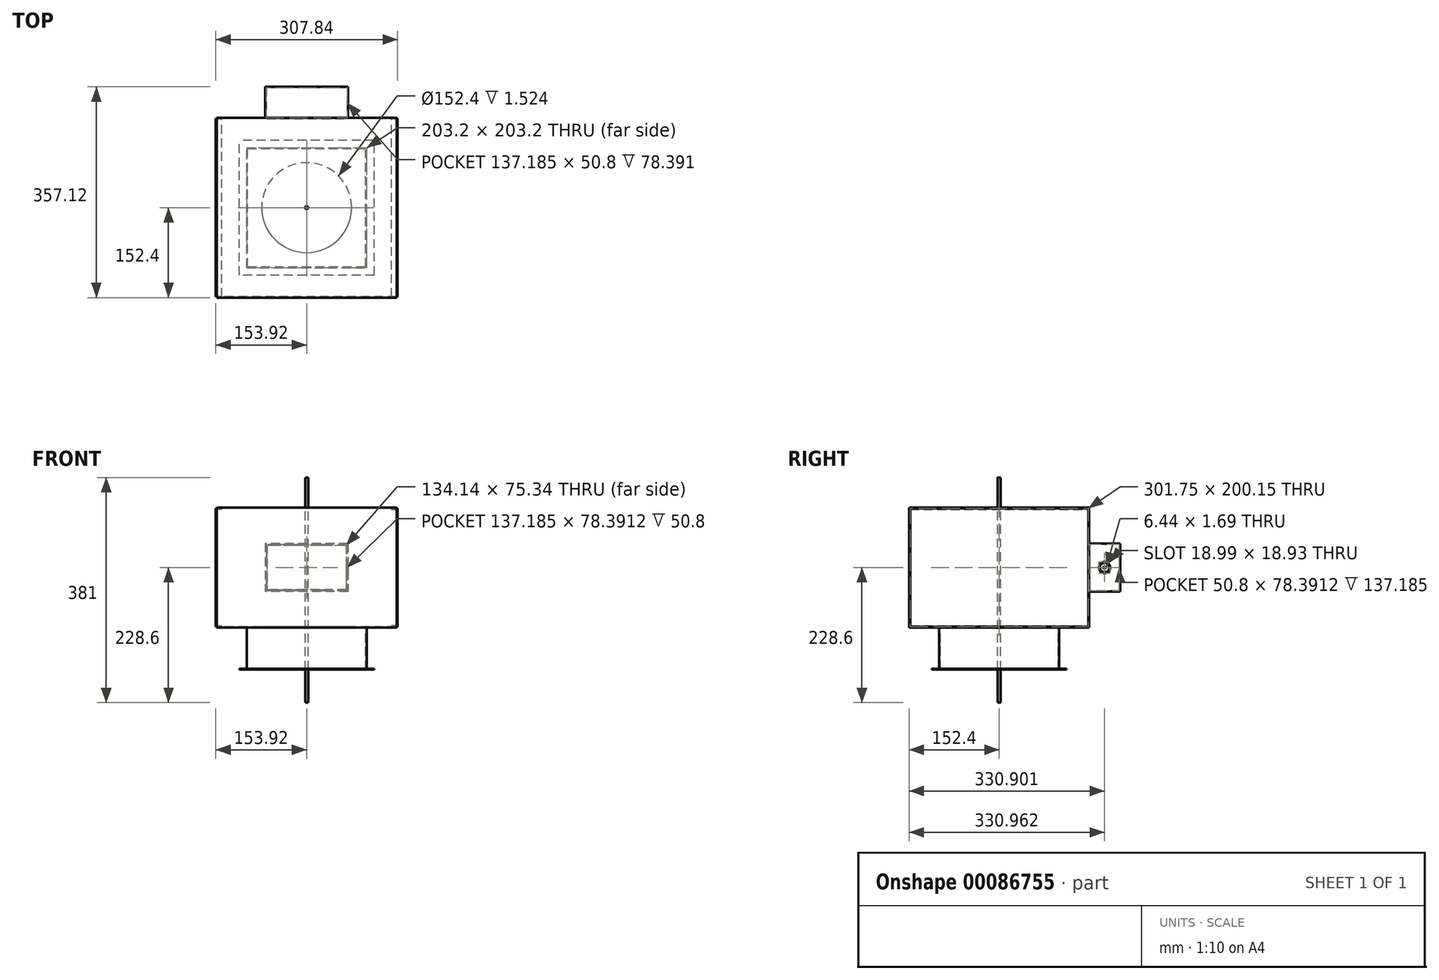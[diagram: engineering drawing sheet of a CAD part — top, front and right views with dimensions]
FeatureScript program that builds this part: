
annotation { "Feature Type Name" : "Feature", "Feature Type Description" : "" }
export const myFeature = defineFeature(function(context is Context, id is Id, definition is map)
    precondition{}
    {
        {
            var Q0;
            Q0=qCreatedBy(makeId("Right.planeOp"),FACE);
            var sketch = newSketch(context, id + "F0", { "sketchPlane" : qUnion([Q0])});
            skLineSegment(sketch, "E0.bottom", {"start": v(-152.4, 101.6) * mm, "end": v(152.4, 101.6) * mm});
            skLineSegment(sketch, "E0.top", {"start": v(-152.4, -101.6) * mm, "end": v(152.4, -101.6) * mm});
            skLineSegment(sketch, "E0.left", {"start": v(-152.4, 101.6) * mm, "end": v(-152.4, -101.6) * mm});
            skLineSegment(sketch, "E0.right", {"start": v(152.4, 101.6) * mm, "end": v(152.4, -101.6) * mm});
            skPoint(sketch, "E0.middle", {"position": v(0, 0) * mm});
            skLineSegment(sketch, "E1.0", {"start": v(-150.88, 100.08) * mm, "end": v(150.88, 100.08) * mm});
            skLineSegment(sketch, "E1.1", {"start": v(-150.88, 100.08) * mm, "end": v(-150.88, -100.08) * mm});
            skLineSegment(sketch, "E1.2", {"start": v(-150.88, -100.08) * mm, "end": v(150.88, -100.08) * mm});
            skLineSegment(sketch, "E1.3", {"start": v(150.88, 100.08) * mm, "end": v(150.88, -100.08) * mm});
            skSolve(sketch);
        }
        {
            var Q0;
            Q0 = qSketchRegion(id + "F0", true);
            extrude(context, id + "F1", {"entities" : qUnion([Q0]), "depth" : 304.8 * mm, "symmetric" : true});
        }
        {
            var Q0;
            Q0=qCreatedBy(makeId("Front.planeOp"),FACE);
            var sketch = newSketch(context, id + "F2", { "sketchPlane" : qUnion([Q0])});
            skLineSegment(sketch, "E2", {"start": v(-143.76, 100.08) * mm, "end": v(-153.92, 100.08) * mm});
            skLineSegment(sketch, "E3", {"start": v(-153.92, 100.08) * mm, "end": v(-153.92, -100.08) * mm});
            skLineSegment(sketch, "E4", {"start": v(-153.92, -100.08) * mm, "end": v(-143.76, -100.08) * mm});
            skLineSegment(sketch, "E5", {"start": v(0, 0) * mm, "end": v(-116.76, 0) * mm, "construction": true});
            skLineSegment(sketch, "E6", {"start": v(0, 0) * mm, "end": v(0, 86.38) * mm, "construction": true});
            skLineSegment(sketch, "E7.0", {"start": v(-152.4, -98.55) * mm, "end": v(-143.76, -98.55) * mm});
            skLineSegment(sketch, "E7.1", {"start": v(-152.4, 98.55) * mm, "end": v(-152.4, -98.55) * mm});
            skLineSegment(sketch, "E7.2", {"start": v(-143.76, 98.55) * mm, "end": v(-152.4, 98.55) * mm});
            skLineSegment(sketch, "E8", {"start": v(-143.76, 98.55) * mm, "end": v(-143.76, 100.08) * mm});
            skLineSegment(sketch, "E9", {"start": v(-143.76, -100.08) * mm, "end": v(-143.76, -98.55) * mm});
            skLineSegment(sketch, "E10.MirrorCS", {"start": v(143.76, 98.55) * mm, "end": v(143.76, 100.08) * mm});
            skLineSegment(sketch, "E11.MirrorCS", {"start": v(143.76, -100.08) * mm, "end": v(143.76, -98.55) * mm});
            skLineSegment(sketch, "E12.MirrorCS", {"start": v(152.4, -98.55) * mm, "end": v(143.76, -98.55) * mm});
            skLineSegment(sketch, "E13.MirrorCS", {"start": v(153.92, -100.08) * mm, "end": v(143.76, -100.08) * mm});
            skLineSegment(sketch, "E14.MirrorCS", {"start": v(143.76, 98.55) * mm, "end": v(152.4, 98.55) * mm});
            skLineSegment(sketch, "E15.MirrorCS", {"start": v(152.4, 98.55) * mm, "end": v(152.4, -98.55) * mm});
            skLineSegment(sketch, "E16.MirrorCS", {"start": v(143.76, 100.08) * mm, "end": v(153.92, 100.08) * mm});
            skLineSegment(sketch, "E17.MirrorCS", {"start": v(153.92, 100.08) * mm, "end": v(153.92, -100.08) * mm});
            skSolve(sketch);
        }
        {
            var Q0;
            Q0 = qSketchRegion(id + "F2", true);
            extrude(context, id + "F3", {"entities" : qUnion([Q0]), "depth" : 301.75 * mm, "symmetric" : true});
        }
        {
            var Q0;
            Q0=makeQuery(id+"F1.opExtrude","SWEPT_FACE",FACE,{"disambiguationData":[OSD([sQuery(id+"F0.wireOp",EDGE,"E0.top")])]});
            var sketch = newSketch(context, id + "F4", { "sketchPlane" : qUnion([Q0])});
            skCircle(sketch, "E18", {"center": v(0, 0) * mm, "radius": 76.2 * mm});
            skSolve(sketch);
        }
        {
            var Q0;
            Q0 = qSketchRegion(id + "F4", true);
            extrude(context, id + "F5", {"entities" : qUnion([Q0]), "operationType" : NewBodyOperationType.REMOVE, "endBound" : BoundingType.UP_TO_NEXT, "oppositeDirection" : true, "depth" : 25.4 * mm});
        }
        {
            var Q0;
            Q0=makeQuery(id+"F1.opExtrude","SWEPT_FACE",FACE,{"disambiguationData":[OSD([sQuery(id+"F0.wireOp",EDGE,"E0.top")])]});
            var sketch = newSketch(context, id + "F6", { "sketchPlane" : qUnion([Q0])});
            skLineSegment(sketch, "E19.bottom", {"start": v(-101.6, 101.6) * mm, "end": v(101.6, 101.6) * mm});
            skLineSegment(sketch, "E19.top", {"start": v(-101.6, -101.6) * mm, "end": v(101.6, -101.6) * mm});
            skLineSegment(sketch, "E19.left", {"start": v(-101.6, 101.6) * mm, "end": v(-101.6, -101.6) * mm});
            skLineSegment(sketch, "E19.right", {"start": v(101.6, 101.6) * mm, "end": v(101.6, -101.6) * mm});
            skPoint(sketch, "E19.middle", {"position": v(0, 0) * mm});
            skLineSegment(sketch, "E20.0", {"start": v(-100.08, 100.08) * mm, "end": v(100.08, 100.08) * mm});
            skLineSegment(sketch, "E20.1", {"start": v(-100.08, 100.08) * mm, "end": v(-100.08, -100.08) * mm});
            skLineSegment(sketch, "E20.2", {"start": v(-100.08, -100.08) * mm, "end": v(100.08, -100.08) * mm});
            skLineSegment(sketch, "E20.3", {"start": v(100.08, 100.08) * mm, "end": v(100.08, -100.08) * mm});
            skSolve(sketch);
        }
        {
            var Q0;
            Q0 = qSketchRegion(id + "F6", true);
            extrude(context, id + "F7", {"entities" : qUnion([Q0]), "operationType" : NewBodyOperationType.ADD, "depth" : 69.85 * mm});
        }
        {
            var Q0;
            Q0=makeQuery(id+"F7.opExtrude","CAP_FACE",FACE,{"disambiguationData":[OSD([sQuery(id+"F6.wireOp",EDGE,"E19.bottom"),sQuery(id+"F6.wireOp",EDGE,"E19.top"),sQuery(id+"F6.wireOp",EDGE,"E19.left"),sQuery(id+"F6.wireOp",EDGE,"E19.right"),sQuery(id+"F6.wireOp",EDGE,"E20.0"),sQuery(id+"F6.wireOp",EDGE,"E20.1"),sQuery(id+"F6.wireOp",EDGE,"E20.2"),sQuery(id+"F6.wireOp",EDGE,"E20.3")])],"isStart":false});
            var sketch = newSketch(context, id + "F8", { "sketchPlane" : qUnion([Q0])});
            skLineSegment(sketch, "E21.bottom", {"start": v(114.3, 114.3) * mm, "end": v(-114.3, 114.3) * mm});
            skLineSegment(sketch, "E21.top", {"start": v(114.3, -114.3) * mm, "end": v(-114.3, -114.3) * mm});
            skLineSegment(sketch, "E21.left", {"start": v(114.3, 114.3) * mm, "end": v(114.3, -114.3) * mm});
            skLineSegment(sketch, "E21.right", {"start": v(-114.3, 114.3) * mm, "end": v(-114.3, -114.3) * mm});
            skPoint(sketch, "E21.middle", {"position": v(0, 0) * mm});
            skLineSegment(sketch, "E22.bottom", {"start": v(100.08, 100.08) * mm, "end": v(-100.08, 100.08) * mm});
            skLineSegment(sketch, "E22.top", {"start": v(100.08, -100.08) * mm, "end": v(-100.08, -100.08) * mm});
            skLineSegment(sketch, "E22.left", {"start": v(100.08, 100.08) * mm, "end": v(100.08, -100.08) * mm});
            skLineSegment(sketch, "E22.right", {"start": v(-100.08, 100.08) * mm, "end": v(-100.08, -100.08) * mm});
            skSolve(sketch);
        }
        {
            var Q0;
            Q0 = qSketchRegion(id + "F8", true);
            extrude(context, id + "F9", {"entities" : qUnion([Q0]), "operationType" : NewBodyOperationType.ADD, "depth" : 1.52 * mm});
        }
        {
            var Q0;
            Q0=makeQuery(id+"F1.opExtrude","SWEPT_FACE",FACE,{"disambiguationData":[OSD([sQuery(id+"F0.wireOp",EDGE,"E0.right")])]});
            var sketch = newSketch(context, id + "F10", { "sketchPlane" : qUnion([Q0])});
            skLineSegment(sketch, "E23.bottom", {"start": v(-67.07, 37.67) * mm, "end": v(67.07, 37.67) * mm});
            skLineSegment(sketch, "E23.top", {"start": v(-67.07, -37.67) * mm, "end": v(67.07, -37.67) * mm});
            skLineSegment(sketch, "E23.left", {"start": v(-67.07, 37.67) * mm, "end": v(-67.07, -37.67) * mm});
            skLineSegment(sketch, "E23.right", {"start": v(67.07, 37.67) * mm, "end": v(67.07, -37.67) * mm});
            skPoint(sketch, "E23.middle", {"position": v(0, 0) * mm});
            skSolve(sketch);
        }
        {
            var Q0;
            Q0 = qSketchRegion(id + "F10", true);
            extrude(context, id + "F11", {"entities" : qUnion([Q0]), "operationType" : NewBodyOperationType.REMOVE, "endBound" : BoundingType.UP_TO_NEXT, "oppositeDirection" : true, "depth" : 25.4 * mm});
        }
        {
            var Q0;
            Q0=makeQuery(id+"F1.opExtrude","SWEPT_FACE",FACE,{"disambiguationData":[OSD([sQuery(id+"F0.wireOp",EDGE,"E0.right")])]});
            var sketch = newSketch(context, id + "F12", { "sketchPlane" : qUnion([Q0])});
            skLineSegment(sketch, "E24.bottom", {"start": v(-68.6, 39.2) * mm, "end": v(68.6, 39.2) * mm});
            skLineSegment(sketch, "E24.top", {"start": v(-68.6, -39.2) * mm, "end": v(68.6, -39.2) * mm});
            skLineSegment(sketch, "E24.left", {"start": v(-68.6, 39.2) * mm, "end": v(-68.6, -39.2) * mm});
            skLineSegment(sketch, "E24.right", {"start": v(68.6, 39.2) * mm, "end": v(68.6, -39.2) * mm});
            skPoint(sketch, "E24.middle", {"position": v(0, 0) * mm});
            skLineSegment(sketch, "E25.0", {"start": v(-70.12, 40.72) * mm, "end": v(70.12, 40.72) * mm});
            skLineSegment(sketch, "E25.1", {"start": v(-70.12, 40.72) * mm, "end": v(-70.12, -40.72) * mm});
            skLineSegment(sketch, "E25.2", {"start": v(-70.12, -40.72) * mm, "end": v(70.12, -40.72) * mm});
            skLineSegment(sketch, "E25.3", {"start": v(70.12, 40.72) * mm, "end": v(70.12, -40.72) * mm});
            skSolve(sketch);
        }
        {
            var Q0;
            Q0 = qSketchRegion(id + "F12", true);
            extrude(context, id + "F13", {"entities" : qUnion([Q0]), "operationType" : NewBodyOperationType.ADD, "depth" : 50.8 * mm});
        }
        {
            var Q0;
            Q0=makeQuery(id+"F13.opExtrude","CAP_FACE",FACE,{"disambiguationData":[OSD([sQuery(id+"F12.wireOp",EDGE,"E24.bottom"),sQuery(id+"F12.wireOp",EDGE,"E24.top"),sQuery(id+"F12.wireOp",EDGE,"E24.left"),sQuery(id+"F12.wireOp",EDGE,"E24.right"),sQuery(id+"F12.wireOp",EDGE,"E25.0"),sQuery(id+"F12.wireOp",EDGE,"E25.1"),sQuery(id+"F12.wireOp",EDGE,"E25.2"),sQuery(id+"F12.wireOp",EDGE,"E25.3")])],"isStart":false});
            var sketch = newSketch(context, id + "F14", { "sketchPlane" : qUnion([Q0])});
            skLineSegment(sketch, "E26.bottom", {"start": v(-70.12, 40.72) * mm, "end": v(70.12, 40.72) * mm});
            skLineSegment(sketch, "E26.top", {"start": v(-70.12, -40.72) * mm, "end": v(70.12, -40.72) * mm});
            skLineSegment(sketch, "E26.left", {"start": v(-70.12, 40.72) * mm, "end": v(-70.12, -40.72) * mm});
            skLineSegment(sketch, "E26.right", {"start": v(70.12, 40.72) * mm, "end": v(70.12, -40.72) * mm});
            skSolve(sketch);
        }
        {
            var Q0;
            Q0 = qSketchRegion(id + "F14", true);
            extrude(context, id + "F15", {"entities" : qUnion([Q0]), "operationType" : NewBodyOperationType.ADD, "depth" : 1.52 * mm});
        }
        {
            var Q0;
            Q0=makeQuery(id+"F15.boolean.opBoolean","MERGE",FACE,{"derivedFrom":[makeQuery(id+"F13.opExtrude","SWEPT_FACE",FACE,{"disambiguationData":[OSD([sQuery(id+"F12.wireOp",EDGE,"E25.1")])]}),makeQuery(id+"F15.opExtrude","SWEPT_FACE",FACE,{"disambiguationData":[OSD([sQuery(id+"F14.wireOp",EDGE,"E26.left")])]})]});
            var sketch = newSketch(context, id + "F16", { "sketchPlane" : qUnion([Q0])});
            skArc(sketch, "E27", {"start": v(187.96, 1.52) * mm, "mid": v(169.04, 0) * mm, "end": v(187.96, -1.52) * mm});
            skLineSegment(sketch, "E28", {"start": v(178.56, 40.72) * mm, "end": v(178.56, -40.72) * mm, "construction": true});
            skArc(sketch, "E29", {"start": v(186.42, 1.52) * mm, "mid": v(170.56, 0) * mm, "end": v(186.42, -1.52) * mm});
            skLineSegment(sketch, "E30", {"start": v(186.42, 1.52) * mm, "end": v(187.96, 1.52) * mm});
            skLineSegment(sketch, "E31", {"start": v(178.56, 0) * mm, "end": v(198.23, 0) * mm, "construction": true});
            skLineSegment(sketch, "E32.MirrorCS", {"start": v(186.42, -1.52) * mm, "end": v(187.96, -1.52) * mm});
            skLineSegment(sketch, "E33.bottom", {"start": v(175.34, -0.84) * mm, "end": v(181.78, -0.84) * mm});
            skLineSegment(sketch, "E33.top", {"start": v(175.34, 0.84) * mm, "end": v(181.78, 0.84) * mm});
            skLineSegment(sketch, "E33.left", {"start": v(175.34, -0.84) * mm, "end": v(175.34, 0.84) * mm});
            skLineSegment(sketch, "E33.right", {"start": v(181.78, -0.84) * mm, "end": v(181.78, 0.84) * mm});
            skSolve(sketch);
        }
        {
            var Q0;
            Q0 = qSketchRegion(id + "F16", true);
            extrude(context, id + "F17", {"entities" : qUnion([Q0]), "operationType" : NewBodyOperationType.REMOVE, "endBound" : BoundingType.UP_TO_NEXT, "oppositeDirection" : true, "depth" : 25.4 * mm});
        }
        {
            var Q0;
            Q0=qCreatedBy(makeId("Right.planeOp"),FACE);
            var sketch = newSketch(context, id + "F18", { "sketchPlane" : qUnion([Q0])});
            skLineSegment(sketch, "E34", {"start": v(0, -228.6) * mm, "end": v(0, 152.4) * mm, "construction": true});
            skLineSegment(sketch, "E35.bottom", {"start": v(0, 152.4) * mm, "end": v(2.54, 152.4) * mm});
            skLineSegment(sketch, "E35.top", {"start": v(0, -228.6) * mm, "end": v(2.54, -228.6) * mm});
            skLineSegment(sketch, "E35.left", {"start": v(0, 152.4) * mm, "end": v(0, -228.6) * mm});
            skLineSegment(sketch, "E35.right", {"start": v(2.54, 152.4) * mm, "end": v(2.54, -228.6) * mm});
            skSolve(sketch);
        }
        {
            var Q0;
            Q0 = qSketchRegion(id + "F18", true);
            var Q1;
            Q1=sQuery(id+"F18.wireOp",EDGE,"E35.left");
            revolve(context, id + "F19", {"entities" : qUnion([Q0]), "axis" : qUnion([Q1]), "revolveType" : RevolveType.FULL});
        }
    });
